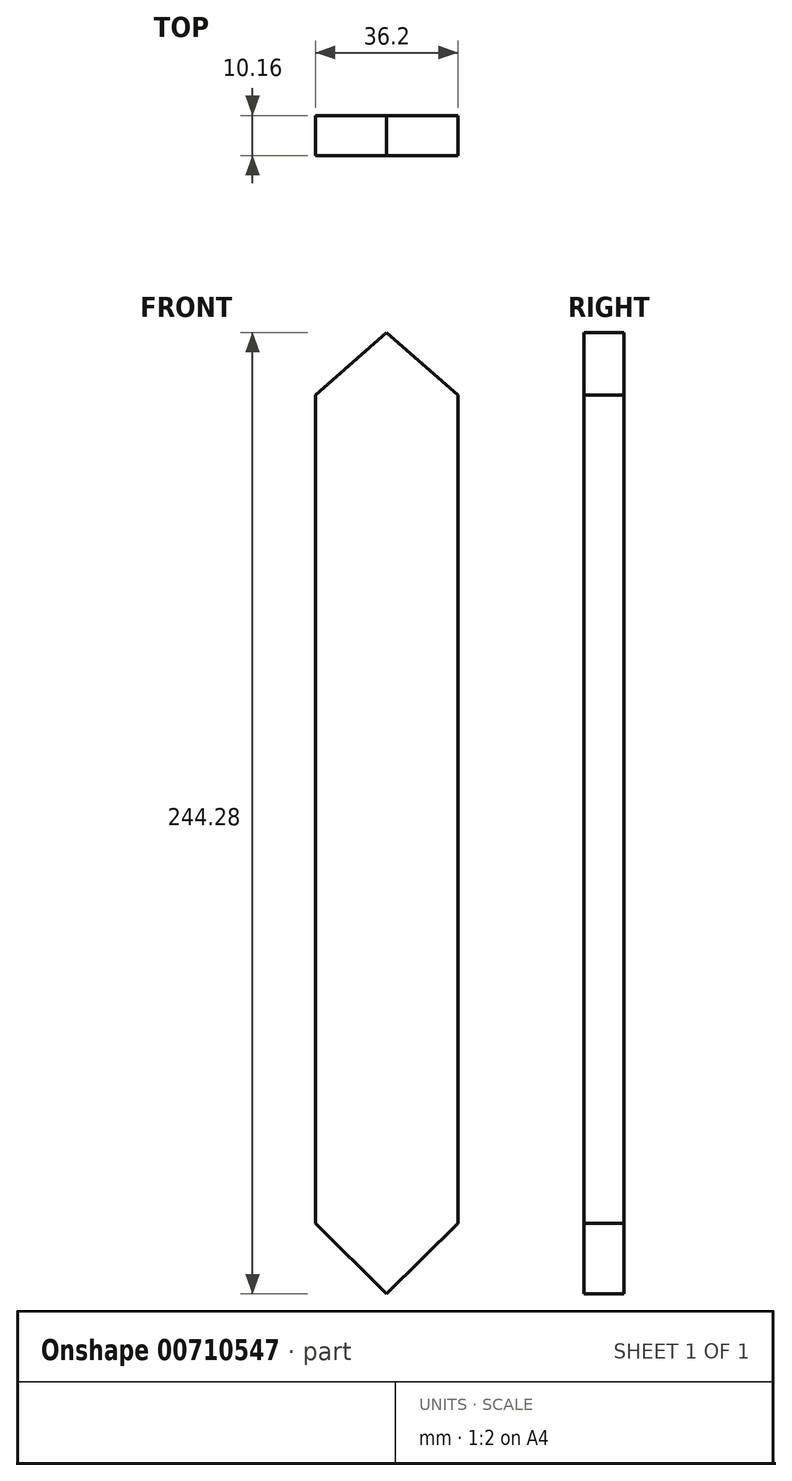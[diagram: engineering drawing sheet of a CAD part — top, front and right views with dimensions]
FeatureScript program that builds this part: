
annotation { "Feature Type Name" : "Feature", "Feature Type Description" : "" }
export const myFeature = defineFeature(function(context is Context, id is Id, definition is map)
    precondition{}
    {
        {
            var Q0;
            Q0=qCreatedBy(makeId("Front.planeOp"),FACE);
            var sketch = newSketch(context, id + "F0", { "sketchPlane" : qUnion([Q0])});
            skFitSpline(sketch, "E0", {"points": [v(-58.77, 10.9) * mm, v(-52.04, 16.33) * mm, v(-46.35, 20.47) * mm, v(-42.08, 21.5) * mm, v(-37.3, 20.2) * mm, v(-33.15, 18) * mm], "startDerivative": vector(27.97, 22.48) * mm, "endDerivative": vector(22.23, -12.93) * mm});
            skLineSegment(sketch, "E1", {"start": v(-33.15, 18) * mm, "end": v(0, 0) * mm});
            skLineSegment(sketch, "E2", {"start": v(0, 0) * mm, "end": v(0, 6.5) * mm});
            skLineSegment(sketch, "E3", {"start": v(-58.77, 10.9) * mm, "end": v(-52.17, 34.44) * mm});
            skFitSpline(sketch, "E4", {"points": [v(-52.17, 34.44) * mm, v(-48.35, 40.7) * mm, v(-44.15, 44.9) * mm, v(-40.76, 45.72) * mm, v(-37.26, 44.79) * mm], "startDerivative": vector(11.84, 21.29) * mm, "endDerivative": vector(16.46, -5.96) * mm});
            skLineSegment(sketch, "E5", {"start": v(-37.26, 44.79) * mm, "end": v(-12.38, 31.59) * mm});
            skFitSpline(sketch, "E6", {"points": [v(-12.38, 31.59) * mm, v(-11.57, 45.95) * mm, v(-12.01, 59.35) * mm, v(-13.24, 72.07) * mm, v(-15.2, 81.42) * mm, v(-20.04, 98.98) * mm, v(-23.62, 110.2) * mm, v(-26.8, 116.07) * mm], "startDerivative": vector(7.18, 93.5) * mm, "endDerivative": vector(-31.36, 51.49) * mm});
            skFitSpline(sketch, "E7", {"points": [v(-26.8, 116.07) * mm, v(-28.43, 135.58) * mm, v(-30.56, 161.2) * mm, v(-33.27, 195.81) * mm, v(-36.38, 226.72) * mm, v(-36.58, 228.72) * mm, v(-36.26, 231.14) * mm, v(-34.94, 240.06) * mm, v(-32.21, 267.55) * mm, v(-29.1, 299.32) * mm, v(-26.8, 324.09) * mm, v(-26.1, 336.42) * mm], "startDerivative": vector(-16.49, 198.18) * mm, "endDerivative": vector(6.55, 149.17) * mm});
            skLineSegment(sketch, "E8", {"start": v(-26.1, 336.42) * mm, "end": v(0, 384.5) * mm});
            skLineSegment(sketch, "E9.MirrorCS", {"start": v(33.15, 18) * mm, "end": v(0, 0) * mm});
            skFitSpline(sketch, "E10.MirrorCS", {"points": [v(58.77, 10.9) * mm, v(52.04, 16.33) * mm, v(46.35, 20.47) * mm, v(42.08, 21.5) * mm, v(37.3, 20.2) * mm, v(33.15, 18) * mm], "startDerivative": vector(-27.97, 22.48) * mm, "endDerivative": vector(-22.23, -12.93) * mm});
            skLineSegment(sketch, "E11.MirrorCS", {"start": v(37.26, 44.79) * mm, "end": v(12.38, 31.59) * mm});
            skLineSegment(sketch, "E12.MirrorCS", {"start": v(58.77, 10.9) * mm, "end": v(52.17, 34.44) * mm});
            skFitSpline(sketch, "E13.MirrorCS", {"points": [v(52.17, 34.44) * mm, v(48.35, 40.7) * mm, v(44.15, 44.9) * mm, v(40.76, 45.72) * mm, v(37.26, 44.79) * mm], "startDerivative": vector(-11.84, 21.29) * mm, "endDerivative": vector(-16.46, -5.96) * mm});
            skFitSpline(sketch, "E14.MirrorCS", {"points": [v(12.38, 31.59) * mm, v(11.57, 45.95) * mm, v(12.01, 59.35) * mm, v(13.24, 72.07) * mm, v(15.2, 81.42) * mm, v(20.04, 98.98) * mm, v(23.62, 110.2) * mm, v(26.8, 116.07) * mm], "startDerivative": vector(-7.18, 93.5) * mm, "endDerivative": vector(31.36, 51.49) * mm});
            skFitSpline(sketch, "E15.MirrorCS", {"points": [v(26.8, 116.07) * mm, v(28.43, 135.58) * mm, v(30.56, 161.2) * mm, v(33.27, 195.81) * mm, v(36.38, 226.72) * mm, v(36.58, 228.72) * mm, v(36.26, 231.14) * mm, v(34.94, 240.06) * mm, v(32.21, 267.55) * mm, v(29.1, 299.32) * mm, v(26.8, 324.09) * mm, v(26.1, 336.42) * mm], "startDerivative": vector(16.49, 198.18) * mm, "endDerivative": vector(-6.55, 149.17) * mm});
            skLineSegment(sketch, "E16.MirrorCS", {"start": v(26.1, 336.42) * mm, "end": v(0, 384.5) * mm});
            skSolve(sketch);
        }
        {
            var Q0;
            Q0=makeQuery(id+"F0.imprint","IMPRINT",FACE,{"disambiguationData":[TD([[makeQuery(id+"F0.imprint","IMPRINT",EDGE,{"derivedFrom":sQuery(id+"F0.wireOp",EDGE,"E0")}),1.0]])]});
            extrude(context, id + "F1", {"entities" : qUnion([Q0]), "endBound" : BoundingType.SYMMETRIC, "depth" : 10.16 * mm, "offsetDistance" : 25.4 * mm});
        }
        {
            var Q0;
            Q0=makeQuery(id+"F1.opExtrude","CAP_FACE",FACE,{"disambiguationData":[OSD([sQuery(id+"F0.wireOp",EDGE,"E0"),sQuery(id+"F0.wireOp",EDGE,"E1"),sQuery(id+"F0.wireOp",EDGE,"E3"),sQuery(id+"F0.wireOp",EDGE,"E4"),sQuery(id+"F0.wireOp",EDGE,"E5"),sQuery(id+"F0.wireOp",EDGE,"E6"),sQuery(id+"F0.wireOp",EDGE,"E7"),sQuery(id+"F0.wireOp",EDGE,"E8"),sQuery(id+"F0.wireOp",EDGE,"E9.MirrorCS"),sQuery(id+"F0.wireOp",EDGE,"E10.MirrorCS"),sQuery(id+"F0.wireOp",EDGE,"E11.MirrorCS"),sQuery(id+"F0.wireOp",EDGE,"E12.MirrorCS"),sQuery(id+"F0.wireOp",EDGE,"E13.MirrorCS"),sQuery(id+"F0.wireOp",EDGE,"E14.MirrorCS"),sQuery(id+"F0.wireOp",EDGE,"E15.MirrorCS"),sQuery(id+"F0.wireOp",EDGE,"E16.MirrorCS")])],"isStart":true});
            var Q1;
            Q1=makeQuery(id+"F1.opExtrude","CAP_FACE",FACE,{"disambiguationData":[OSD([sQuery(id+"F0.wireOp",EDGE,"E0"),sQuery(id+"F0.wireOp",EDGE,"E1"),sQuery(id+"F0.wireOp",EDGE,"E3"),sQuery(id+"F0.wireOp",EDGE,"E4"),sQuery(id+"F0.wireOp",EDGE,"E5"),sQuery(id+"F0.wireOp",EDGE,"E6"),sQuery(id+"F0.wireOp",EDGE,"E7"),sQuery(id+"F0.wireOp",EDGE,"E8"),sQuery(id+"F0.wireOp",EDGE,"E9.MirrorCS"),sQuery(id+"F0.wireOp",EDGE,"E10.MirrorCS"),sQuery(id+"F0.wireOp",EDGE,"E11.MirrorCS"),sQuery(id+"F0.wireOp",EDGE,"E12.MirrorCS"),sQuery(id+"F0.wireOp",EDGE,"E13.MirrorCS"),sQuery(id+"F0.wireOp",EDGE,"E14.MirrorCS"),sQuery(id+"F0.wireOp",EDGE,"E15.MirrorCS"),sQuery(id+"F0.wireOp",EDGE,"E16.MirrorCS")])],"isStart":false});
            chamfer(context, id + "F2", {"entities" : qUnion([Q0, Q1]), "chamferType" : ChamferType.OFFSET_ANGLE, "width" : 2.54 * mm, "oppositeDirection" : false, "angle" : 45 * degree, "tangentPropagation" : true});
        }
        {
            var Q0;
            Q0=qCreatedBy(makeId("Front.planeOp"),FACE);
            var sketch = newSketch(context, id + "F3", { "sketchPlane" : qUnion([Q0])});
            skLineSegment(sketch, "E17", {"start": v(0, 102.67) * mm, "end": v(18.1, 120.66) * mm});
            skLineSegment(sketch, "E18", {"start": v(18.1, 120.66) * mm, "end": v(18.1, 331.1) * mm});
            skLineSegment(sketch, "E19", {"start": v(18.1, 331.1) * mm, "end": v(0, 346.95) * mm});
            skLineSegment(sketch, "E20", {"start": v(0, 346.95) * mm, "end": v(0, 335.17) * mm});
            skLineSegment(sketch, "E21.MirrorCS", {"start": v(-18.1, 331.1) * mm, "end": v(0, 346.95) * mm});
            skLineSegment(sketch, "E22.MirrorCS", {"start": v(-18.1, 120.66) * mm, "end": v(-18.1, 331.1) * mm});
            skLineSegment(sketch, "E23.MirrorCS", {"start": v(0, 102.67) * mm, "end": v(-18.1, 120.66) * mm});
            skLineSegment(sketch, "E24", {"start": v(145.3, 449.9) * mm, "end": v(223.66, 407.34) * mm});
            skLineSegment(sketch, "E25.bottom", {"start": v(145.3, 436.36) * mm, "end": v(-151.63, 436.36) * mm});
            skLineSegment(sketch, "E25.top", {"start": v(145.3, -37.6) * mm, "end": v(-151.63, -37.6) * mm});
            skLineSegment(sketch, "E25.left", {"start": v(145.3, 436.36) * mm, "end": v(145.3, -37.6) * mm});
            skLineSegment(sketch, "E25.right", {"start": v(-151.63, 436.36) * mm, "end": v(-151.63, -37.6) * mm});
            skSolve(sketch);
        }
        {
            var Q0;
            Q0=makeQuery(id+"F3.imprint","IMPRINT",FACE,{"disambiguationData":[TD([[makeQuery(id+"F3.imprint","IMPRINT",EDGE,{"derivedFrom":sQuery(id+"F3.wireOp",EDGE,"E17")}),-1.0]])]});
            extrude(context, id + "F4", {"entities" : qUnion([Q0]), "operationType" : NewBodyOperationType.REMOVE, "oppositeDirection" : true, "depth" : 25.4 * mm, "offsetDistance" : 25.4 * mm});
        }
        {
            var Q0;
            Q0=makeQuery(id+"F4.boolean.opBoolean","COPY",FACE,{"derivedFrom":makeQuery(id+"F4.opExtrude","CAP_FACE",FACE,{"disambiguationData":[OSD([sQuery(id+"F3.wireOp",EDGE,"E17"),sQuery(id+"F3.wireOp",EDGE,"E18"),sQuery(id+"F3.wireOp",EDGE,"E19"),sQuery(id+"F3.wireOp",EDGE,"E21.MirrorCS"),sQuery(id+"F3.wireOp",EDGE,"E22.MirrorCS"),sQuery(id+"F3.wireOp",EDGE,"E23.MirrorCS"),sQuery(id+"F3.wireOp",EDGE,"E25.bottom"),sQuery(id+"F3.wireOp",EDGE,"E25.top"),sQuery(id+"F3.wireOp",EDGE,"E25.left"),sQuery(id+"F3.wireOp",EDGE,"E25.right")])],"isStart":true})});
            extrude(context, id + "F5", {"entities" : qUnion([Q0]), "operationType" : NewBodyOperationType.REMOVE, "oppositeDirection" : true, "depth" : 25.4 * mm, "offsetDistance" : 25.4 * mm});
        }
    });
